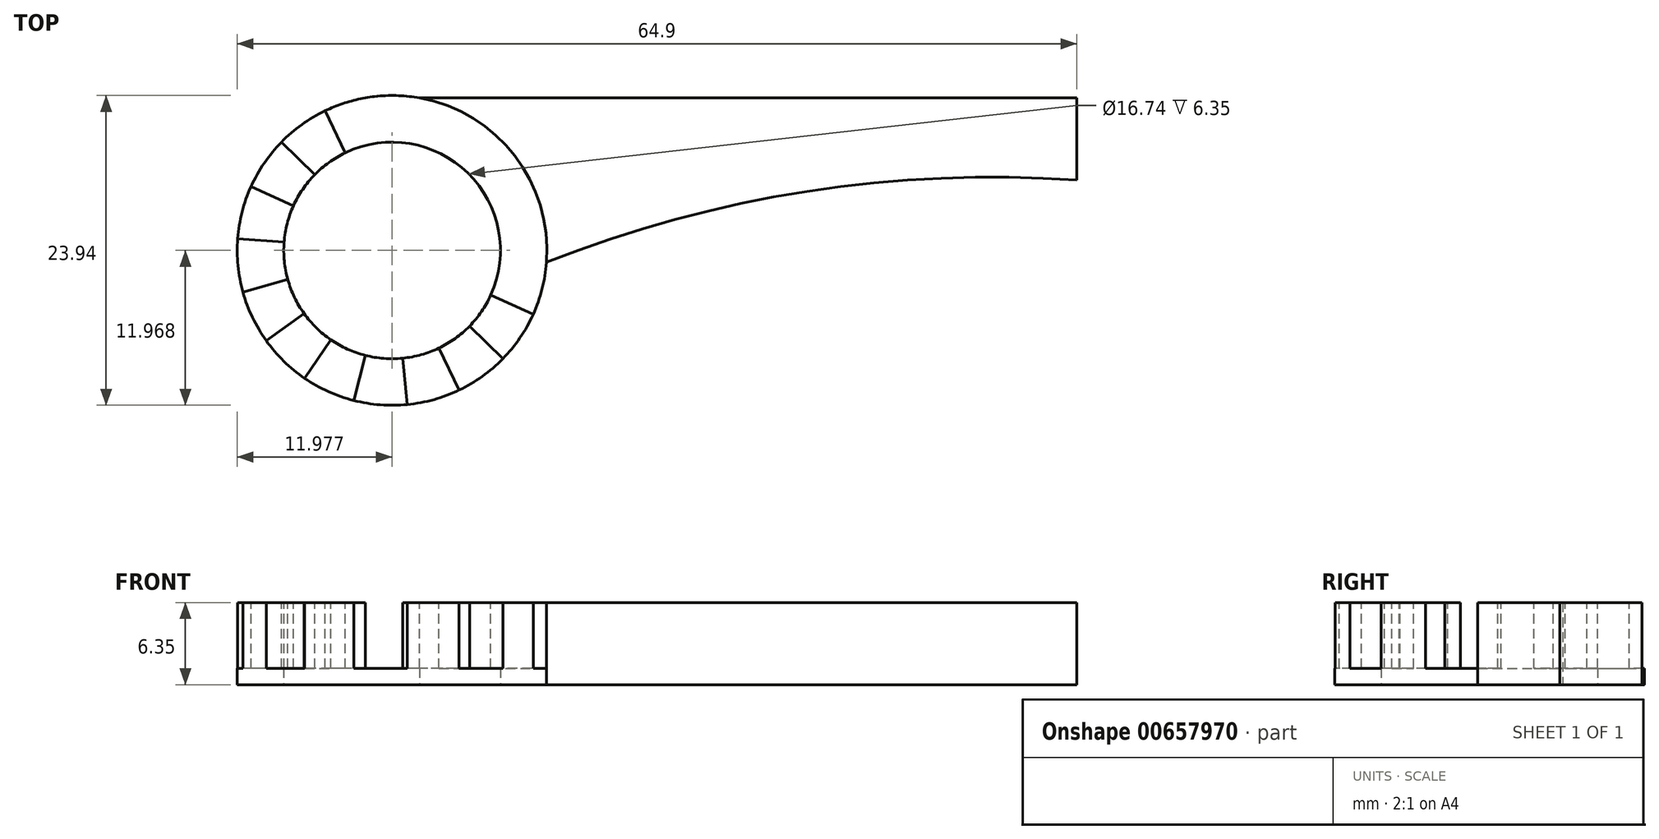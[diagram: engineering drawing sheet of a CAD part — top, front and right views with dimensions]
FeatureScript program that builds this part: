
annotation { "Feature Type Name" : "Feature", "Feature Type Description" : "" }
export const myFeature = defineFeature(function(context is Context, id is Id, definition is map)
    precondition{}
    {
        {
            var Q0;
            Q0=qCreatedBy(makeId("Top.planeOp"),FACE);
            var sketch = newSketch(context, id + "F0", { "sketchPlane" : qUnion([Q0])});
            skLineSegment(sketch, "E0", {"start": v(-12.61, 8.8) * mm, "end": v(38.19, 8.8) * mm});
            skLineSegment(sketch, "E1", {"start": v(38.19, 8.8) * mm, "end": v(38.19, 2.45) * mm});
            skPoint(sketch, "E2.start.orphan", {"position": v(-12.61, 2.45) * mm});
            skPoint(sketch, "E3.end.orphan", {"position": v(-25.4, 8.8) * mm});
            skArc(sketch, "E4", {"start": v(-12.61, 8.8) * mm, "mid": v(-24.2, -10.3) * mm, "end": v(-2.8, -3.9) * mm});
            skPoint(sketch, "E4.third.point", {"position": v(-23.9, -10.68) * mm});
            skArc(sketch, "E5", {"start": v(38.19, 2.45) * mm, "mid": v(17.34, 1.58) * mm, "end": v(-2.8, -3.9) * mm});
            skPoint(sketch, "E6.orphan", {"position": v(38.19, -3.9) * mm});
            skPoint(sketch, "E7.end.orphan", {"position": v(-12.61, -3.9) * mm});
            skCircle(sketch, "E8", {"center": v(-14.73, -2.98) * mm, "radius": 8.37 * mm});
            skSolve(sketch);
        }
        {
            var Q0;
            Q0=makeQuery(id+"F0.imprint","IMPRINT",FACE,{"disambiguationData":[TD([[makeQuery(id+"F0.imprint","IMPRINT",EDGE,{"derivedFrom":sQuery(id+"F0.wireOp",EDGE,"E0")}),-1.0]])]});
            extrude(context, id + "F1", {"entities" : qUnion([Q0]), "depth" : 6.35 * mm, "offsetDistance" : 25.4 * mm});
        }
        {
            var Q0;
            Q0=makeQuery(id+"F1.opExtrude","CAP_FACE",FACE,{"disambiguationData":[OSD([sQuery(id+"F0.wireOp",EDGE,"E0"),sQuery(id+"F0.wireOp",EDGE,"E1"),sQuery(id+"F0.wireOp",EDGE,"E4"),sQuery(id+"F0.wireOp",EDGE,"E5"),sQuery(id+"F0.wireOp",EDGE,"E8")])],"isStart":false});
            var sketch = newSketch(context, id + "F2", { "sketchPlane" : qUnion([Q0])});
            skSolve(sketch);
        }
        {
            var Q0;
            Q0=makeQuery(id+"F2.imprint","IMPRINT",FACE,{"disambiguationData":[TD([[makeQuery(id+"F2.imprint","IMPRINT",EDGE,{"derivedFrom":makeQuery(id+"F1.opExtrude","CAP_EDGE",EDGE,{"disambiguationData":[OSD([sQuery(id+"F0.wireOp",EDGE,"E0")])],"isStart":false})}),-1.0]])]});
            var sketch = newSketch(context, id + "F3", { "sketchPlane" : qUnion([Q0])});
            skCircle(sketch, "E9", {"center": v(-14.73, -2.98) * mm, "radius": 6.06 * mm});
            skLineSegment(sketch, "E10", {"start": v(-14.73, -2.98) * mm, "end": v(0, -4.1) * mm});
            skLineSegment(sketch, "E11.3.0", {"start": v(-14.73, -2.98) * mm, "end": v(-21.12, 10.34) * mm});
            skLineSegment(sketch, "E11.4.0", {"start": v(-14.73, -2.98) * mm, "end": v(-28.2, 3.12) * mm});
            skLineSegment(sketch, "E11.5.0", {"start": v(-14.73, -2.98) * mm, "end": v(-28.96, -6.96) * mm});
            skLineSegment(sketch, "E11.6.0", {"start": v(-14.73, -2.98) * mm, "end": v(-23.08, -15.18) * mm});
            skLineSegment(sketch, "E11.7.0", {"start": v(-14.73, -2.98) * mm, "end": v(-13.29, -17.69) * mm});
            skLineSegment(sketch, "E11.8.0", {"start": v(-14.73, -2.98) * mm, "end": v(-4.17, -13.32) * mm});
            skLineSegment(sketch, "E12", {"start": v(-14.73, -2.98) * mm, "end": v(0, -9.66) * mm});
            skLineSegment(sketch, "E13.3.0", {"start": v(-14.73, -2.98) * mm, "end": v(-16.32, 13.12) * mm});
            skLineSegment(sketch, "E13.4.0", {"start": v(-14.73, -2.98) * mm, "end": v(-26.3, 8.33) * mm});
            skLineSegment(sketch, "E13.5.0", {"start": v(-14.73, -2.98) * mm, "end": v(-30.86, -1.75) * mm});
            skLineSegment(sketch, "E13.6.0", {"start": v(-14.73, -2.98) * mm, "end": v(-27.88, -12.4) * mm});
            skLineSegment(sketch, "E13.7.0", {"start": v(-14.73, -2.98) * mm, "end": v(-18.75, -18.65) * mm});
            skLineSegment(sketch, "E13.8.0", {"start": v(-14.73, -2.98) * mm, "end": v(-7.74, -17.57) * mm});
            skLineSegment(sketch, "E14", {"start": v(0, -4.1) * mm, "end": v(0, -9.66) * mm});
            skLineSegment(sketch, "E15", {"start": v(-4.17, -13.32) * mm, "end": v(-7.74, -17.57) * mm});
            skLineSegment(sketch, "E16", {"start": v(-13.29, -17.69) * mm, "end": v(-18.75, -18.65) * mm});
            skLineSegment(sketch, "E17", {"start": v(-23.08, -15.18) * mm, "end": v(-27.88, -12.4) * mm});
            skLineSegment(sketch, "E18", {"start": v(-28.96, -6.96) * mm, "end": v(-30.86, -1.75) * mm});
            skLineSegment(sketch, "E19", {"start": v(-28.2, 3.12) * mm, "end": v(-26.3, 8.33) * mm});
            skLineSegment(sketch, "E20", {"start": v(-21.12, 10.34) * mm, "end": v(-16.32, 13.12) * mm});
            skSolve(sketch);
        }
        {
            var Q0;
            {var subQ0=sQuery(id+"F3.wireOp",EDGE,"E11.7.0");var subQ1=makeQuery(id+"F2.imprint","IMPRINT",EDGE,{"derivedFrom":makeQuery(id+"F1.opExtrude","CAP_EDGE",EDGE,{"disambiguationData":[OSD([sQuery(id+"F0.wireOp",EDGE,"E4")])],"isStart":false})});var subQ2=makeQuery(id+"F3.imprint","INTERSECT",VERTEX,{"derivedFrom":[subQ1,subQ0]});Q0=makeQuery(id+"F3.imprint","IMPRINT",FACE,{"disambiguationData":[TD([[makeQuery(id+"F3.imprint","IMPRINT",EDGE,{"disambiguationData":[TD([[subQ2,1.0]])],"derivedFrom":subQ0}),-1.0]])]});}
            var Q1;
            {var subQ0=sQuery(id+"F3.wireOp",EDGE,"E11.8.0");var subQ1=makeQuery(id+"F2.imprint","IMPRINT",EDGE,{"derivedFrom":makeQuery(id+"F1.opExtrude","CAP_EDGE",EDGE,{"disambiguationData":[OSD([sQuery(id+"F0.wireOp",EDGE,"E4")])],"isStart":false})});var subQ2=makeQuery(id+"F3.imprint","INTERSECT",VERTEX,{"derivedFrom":[subQ1,subQ0]});Q1=makeQuery(id+"F3.imprint","IMPRINT",FACE,{"disambiguationData":[TD([[makeQuery(id+"F3.imprint","IMPRINT",EDGE,{"disambiguationData":[TD([[subQ2,1.0]])],"derivedFrom":subQ0}),-1.0]])]});}
            var Q2;
            {var subQ0=makeQuery(id+"F2.imprint","IMPRINT",EDGE,{"derivedFrom":makeQuery(id+"F1.opExtrude","CAP_EDGE",EDGE,{"disambiguationData":[OSD([sQuery(id+"F0.wireOp",EDGE,"E5")])],"isStart":false})});var subQ3=sQuery(id+"F3.wireOp",EDGE,"E10");var subQ4=makeQuery(id+"F3.imprint","INTERSECT",VERTEX,{"derivedFrom":[subQ0,subQ3]});Q2=makeQuery(id+"F3.imprint","IMPRINT",FACE,{"disambiguationData":[TD([[makeQuery(id+"F3.imprint","IMPRINT",EDGE,{"disambiguationData":[TD([[subQ4,1.0]])],"derivedFrom":subQ3}),-1.0]])]});}
            var Q3;
            {var subQ0=sQuery(id+"F3.wireOp",EDGE,"E11.6.0");var subQ1=makeQuery(id+"F2.imprint","IMPRINT",EDGE,{"derivedFrom":makeQuery(id+"F1.opExtrude","CAP_EDGE",EDGE,{"disambiguationData":[OSD([sQuery(id+"F0.wireOp",EDGE,"E4")])],"isStart":false})});var subQ2=makeQuery(id+"F3.imprint","INTERSECT",VERTEX,{"derivedFrom":[subQ1,subQ0]});Q3=makeQuery(id+"F3.imprint","IMPRINT",FACE,{"disambiguationData":[TD([[makeQuery(id+"F3.imprint","IMPRINT",EDGE,{"disambiguationData":[TD([[subQ2,1.0]])],"derivedFrom":subQ0}),-1.0]])]});}
            var Q4;
            {var subQ0=sQuery(id+"F3.wireOp",EDGE,"E11.5.0");var subQ1=makeQuery(id+"F2.imprint","IMPRINT",EDGE,{"derivedFrom":makeQuery(id+"F1.opExtrude","CAP_EDGE",EDGE,{"disambiguationData":[OSD([sQuery(id+"F0.wireOp",EDGE,"E4")])],"isStart":false})});var subQ2=makeQuery(id+"F3.imprint","INTERSECT",VERTEX,{"derivedFrom":[subQ1,subQ0]});Q4=makeQuery(id+"F3.imprint","IMPRINT",FACE,{"disambiguationData":[TD([[makeQuery(id+"F3.imprint","IMPRINT",EDGE,{"disambiguationData":[TD([[subQ2,1.0]])],"derivedFrom":subQ0}),-1.0]])]});}
            var Q5;
            {var subQ0=sQuery(id+"F3.wireOp",EDGE,"E11.4.0");var subQ1=makeQuery(id+"F2.imprint","IMPRINT",EDGE,{"derivedFrom":makeQuery(id+"F1.opExtrude","CAP_EDGE",EDGE,{"disambiguationData":[OSD([sQuery(id+"F0.wireOp",EDGE,"E4")])],"isStart":false})});var subQ2=makeQuery(id+"F3.imprint","INTERSECT",VERTEX,{"derivedFrom":[subQ1,subQ0]});Q5=makeQuery(id+"F3.imprint","IMPRINT",FACE,{"disambiguationData":[TD([[makeQuery(id+"F3.imprint","IMPRINT",EDGE,{"disambiguationData":[TD([[subQ2,1.0]])],"derivedFrom":subQ0}),-1.0]])]});}
            var Q6;
            {var subQ0=sQuery(id+"F3.wireOp",EDGE,"E11.3.0");var subQ1=makeQuery(id+"F2.imprint","IMPRINT",EDGE,{"derivedFrom":makeQuery(id+"F1.opExtrude","CAP_EDGE",EDGE,{"disambiguationData":[OSD([sQuery(id+"F0.wireOp",EDGE,"E4")])],"isStart":false})});var subQ2=makeQuery(id+"F3.imprint","INTERSECT",VERTEX,{"derivedFrom":[subQ1,subQ0]});Q6=makeQuery(id+"F3.imprint","IMPRINT",FACE,{"disambiguationData":[TD([[makeQuery(id+"F3.imprint","IMPRINT",EDGE,{"disambiguationData":[TD([[subQ2,1.0]])],"derivedFrom":subQ0}),-1.0]])]});}
            extrude(context, id + "F4", {"entities" : qUnion([Q0, Q1, Q2, Q3, Q4, Q5, Q6]), "operationType" : NewBodyOperationType.REMOVE, "oppositeDirection" : true, "depth" : 5.08 * mm, "offsetDistance" : 25.4 * mm});
        }
        {
            var Q0;
            Q0=makeQuery(id+"F2.imprint","IMPRINT",FACE,{"disambiguationData":[TD([[makeQuery(id+"F2.imprint","IMPRINT",EDGE,{"derivedFrom":makeQuery(id+"F1.opExtrude","CAP_EDGE",EDGE,{"disambiguationData":[OSD([sQuery(id+"F0.wireOp",EDGE,"E0")])],"isStart":false})}),-1.0]])]});
            var sketch = newSketch(context, id + "F5", { "sketchPlane" : qUnion([Q0])});
            skArc(sketch, "E21", {"start": v(-6.48, -3.61) * mm, "mid": v(-8.92, 2.92) * mm, "end": v(-15.49, 5.26) * mm});
            skArc(sketch, "E22", {"start": v(-2.8, -3.9) * mm, "mid": v(-6.34, 5.56) * mm, "end": v(-15.85, 8.94) * mm});
            skLineSegment(sketch, "E23", {"start": v(-15.85, 8.94) * mm, "end": v(-16.26, 8.9) * mm});
            skLineSegment(sketch, "E24", {"start": v(-16.26, 8.9) * mm, "end": v(-15.9, 5.26) * mm});
            skLineSegment(sketch, "E25", {"start": v(-15.9, 5.26) * mm, "end": v(-15.49, 5.26) * mm});
            skLineSegment(sketch, "E26", {"start": v(-6.48, -3.61) * mm, "end": v(-6.48, -3.87) * mm});
            skLineSegment(sketch, "E27", {"start": v(-6.48, -3.87) * mm, "end": v(-2.8, -4.15) * mm});
            skLineSegment(sketch, "E28", {"start": v(-2.8, -4.15) * mm, "end": v(-2.8, -3.9) * mm});
            skSolve(sketch);
        }
        {
            var Q0;
            Q0 = qSketchRegion(id + "F5", true);
            extrude(context, id + "F6", {"entities" : qUnion([Q0]), "operationType" : NewBodyOperationType.REMOVE, "oppositeDirection" : true, "depth" : 5.08 * mm, "offsetDistance" : 25.4 * mm});
        }
    });
